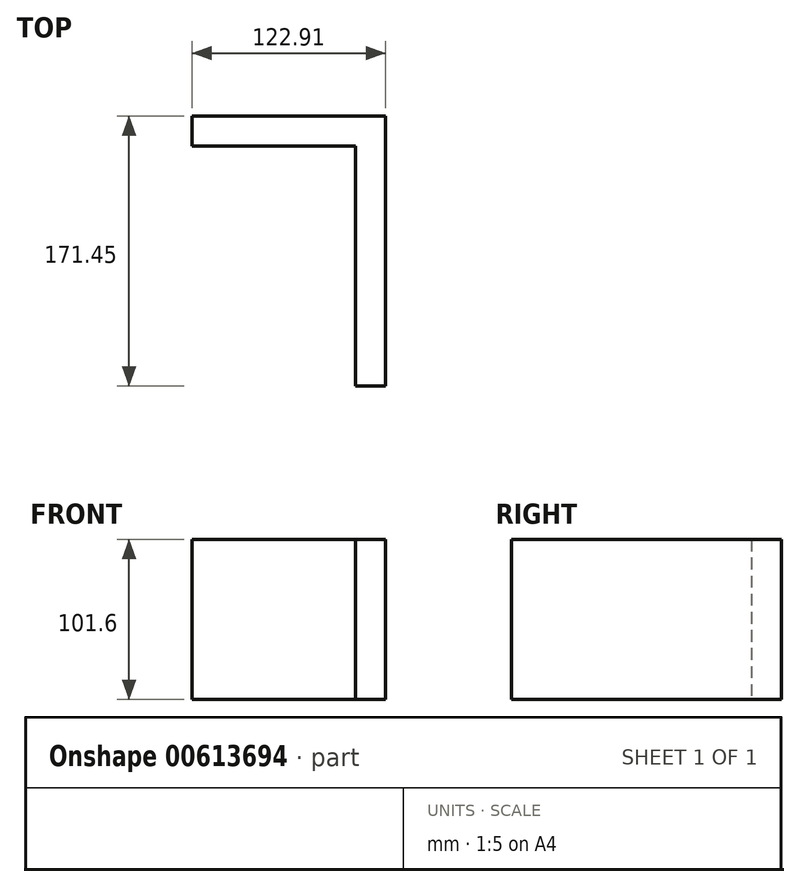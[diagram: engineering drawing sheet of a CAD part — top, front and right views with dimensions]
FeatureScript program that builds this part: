
annotation { "Feature Type Name" : "Feature", "Feature Type Description" : "" }
export const myFeature = defineFeature(function(context is Context, id is Id, definition is map)
    precondition{}
    {
        {
            var Q0;
            Q0=qCreatedBy(makeId("Top.planeOp"),FACE);
            var sketch = newSketch(context, id + "F0", { "sketchPlane" : qUnion([Q0])});
            skLineSegment(sketch, "E0.bottom", {"start": v(0, 0) * mm, "end": v(-122.9, 0) * mm});
            skLineSegment(sketch, "E0.top", {"start": v(0, 19.05) * mm, "end": v(-122.9, 19.05) * mm});
            skLineSegment(sketch, "E0.left", {"start": v(0, 0) * mm, "end": v(0, 19.05) * mm});
            skLineSegment(sketch, "E0.right", {"start": v(-122.9, 0) * mm, "end": v(-122.9, 19.05) * mm});
            skLineSegment(sketch, "E1.bottom", {"start": v(0, 0) * mm, "end": v(19.05, 0) * mm});
            skLineSegment(sketch, "E1.top", {"start": v(0, 152.4) * mm, "end": v(19.05, 152.4) * mm});
            skLineSegment(sketch, "E1.left", {"start": v(0, 0) * mm, "end": v(0, 152.4) * mm});
            skLineSegment(sketch, "E1.right", {"start": v(19.05, 0) * mm, "end": v(19.05, 152.4) * mm});
            skSolve(sketch);
        }
        {
            var Q0;
            {var subQ0=sQuery(id+"F0.wireOp",EDGE,"E0.bottom");Q0=makeQuery(id+"F0.imprint","IMPRINT",FACE,{"disambiguationData":[TD([[makeQuery(id+"F0.imprint","IMPRINT",EDGE,{"derivedFrom":subQ0}),-1.0]])]});}
            extrude(context, id + "F1", {"entities" : qUnion([Q0]), "depth" : 101.6 * mm, "offsetDistance" : 25.4 * mm});
        }
        {
            var Q0;
            Q0=makeQuery(id+"F1.opExtrude","SWEPT_FACE",FACE,{"disambiguationData":[OSD([sQuery(id+"F0.wireOp",EDGE,"E0.bottom")])]});
            var sketch = newSketch(context, id + "F2", { "sketchPlane" : qUnion([Q0])});
            skLineSegment(sketch, "E2.bottom", {"start": v(0, 101.6) * mm, "end": v(-19.05, 101.6) * mm});
            skLineSegment(sketch, "E2.top", {"start": v(0, 0) * mm, "end": v(-19.05, 0) * mm});
            skLineSegment(sketch, "E2.left", {"start": v(0, 101.6) * mm, "end": v(0, 0) * mm});
            skLineSegment(sketch, "E2.right", {"start": v(-19.05, 101.6) * mm, "end": v(-19.05, 0) * mm});
            skLineSegment(sketch, "E3", {"start": v(0, 50.8) * mm, "end": v(-122.9, 50.8) * mm});
            skLineSegment(sketch, "E4", {"start": v(-19.05, 57.15) * mm, "end": v(-19.05, 44.45) * mm});
            skLineSegment(sketch, "E5", {"start": v(0, 52.39) * mm, "end": v(0, 49.21) * mm});
            skLineSegment(sketch, "E6", {"start": v(0, 49.21) * mm, "end": v(0, 52.39) * mm});
            skLineSegment(sketch, "E7", {"start": v(-19.05, 57.15) * mm, "end": v(0, 52.39) * mm});
            skLineSegment(sketch, "E8", {"start": v(-19.05, 44.45) * mm, "end": v(0, 49.21) * mm});
            skLineSegment(sketch, "E9.0.1.0", {"start": v(-19.05, 76.2) * mm, "end": v(0, 71.44) * mm});
            skLineSegment(sketch, "E9.0.1.1", {"start": v(-19.05, 76.2) * mm, "end": v(-19.05, 63.5) * mm});
            skLineSegment(sketch, "E9.0.1.2", {"start": v(0, 68.26) * mm, "end": v(0, 71.44) * mm});
            skLineSegment(sketch, "E9.0.1.3", {"start": v(-19.05, 63.5) * mm, "end": v(0, 68.26) * mm});
            skLineSegment(sketch, "E9.0.2.0", {"start": v(-19.05, 95.25) * mm, "end": v(0, 90.49) * mm});
            skLineSegment(sketch, "E9.0.2.1", {"start": v(-19.05, 95.25) * mm, "end": v(-19.05, 82.55) * mm});
            skLineSegment(sketch, "E9.0.2.2", {"start": v(0, 87.31) * mm, "end": v(0, 90.49) * mm});
            skLineSegment(sketch, "E9.0.2.3", {"start": v(-19.05, 82.55) * mm, "end": v(0, 87.31) * mm});
            skLineSegment(sketch, "E9.0.3.0", {"start": v(-19.05, 114.3) * mm, "end": v(0, 109.54) * mm});
            skLineSegment(sketch, "E9.0.3.1", {"start": v(-19.05, 114.3) * mm, "end": v(-19.05, 101.6) * mm});
            skLineSegment(sketch, "E9.0.3.2", {"start": v(0, 106.36) * mm, "end": v(0, 109.54) * mm});
            skLineSegment(sketch, "E9.0.3.3", {"start": v(-19.05, 101.6) * mm, "end": v(0, 106.36) * mm});
            skLineSegment(sketch, "E9.direction1", {"start": v(-19.05, 44.45) * mm, "end": v(6.35, 44.45) * mm, "construction": true});
            skLineSegment(sketch, "E9.direction2", {"start": v(-19.05, 44.45) * mm, "end": v(-19.05, 63.5) * mm, "construction": true});
            skLineSegment(sketch, "E10.MirrorCS", {"start": v(-19.05, 25.4) * mm, "end": v(0, 30.16) * mm});
            skLineSegment(sketch, "E11.MirrorCS", {"start": v(-19.05, 38.1) * mm, "end": v(0, 33.34) * mm});
            skLineSegment(sketch, "E12.MirrorCS", {"start": v(-19.05, 19.05) * mm, "end": v(0, 14.29) * mm});
            skLineSegment(sketch, "E13.MirrorCS", {"start": v(-19.05, 6.35) * mm, "end": v(0, 11.11) * mm});
            skLineSegment(sketch, "E14.MirrorCS", {"start": v(-19.05, 0) * mm, "end": v(0, -4.76) * mm});
            skLineSegment(sketch, "E15.MirrorCS", {"start": v(-19.05, -12.7) * mm, "end": v(0, -7.94) * mm});
            skLineSegment(sketch, "E16", {"start": v(-19.05, 0) * mm, "end": v(-19.05, -12.7) * mm});
            skLineSegment(sketch, "E17", {"start": v(0, -4.76) * mm, "end": v(0, -7.94) * mm});
            skSolve(sketch);
        }
        {
            var Q0;
            Q0=makeQuery(id+"F2.imprint","IMPRINT",FACE,{"disambiguationData":[TD([[makeQuery(id+"F2.imprint","IMPRINT",EDGE,{"derivedFrom":sQuery(id+"F2.wireOp",EDGE,"E14.MirrorCS")}),-1.0]])]});
            var Q1;
            {var subQ0=sQuery(id+"F2.wireOp",EDGE,"E12.MirrorCS");Q1=makeQuery(id+"F2.imprint","IMPRINT",FACE,{"disambiguationData":[TD([[makeQuery(id+"F2.imprint","IMPRINT",EDGE,{"derivedFrom":subQ0}),-1.0]])]});}
            var Q2;
            Q2=makeQuery(id+"F2.imprint","IMPRINT",FACE,{"disambiguationData":[TD([[makeQuery(id+"F2.imprint","IMPRINT",EDGE,{"derivedFrom":sQuery(id+"F2.wireOp",EDGE,"E9.0.3.0")}),-1.0]])]});
            var Q3;
            Q3=makeQuery(id+"F2.imprint","IMPRINT",FACE,{"disambiguationData":[TD([[makeQuery(id+"F2.imprint","IMPRINT",EDGE,{"derivedFrom":sQuery(id+"F2.wireOp",EDGE,"E9.0.2.0")}),-1.0]])]});
            var Q4;
            Q4=makeQuery(id+"F2.imprint","IMPRINT",FACE,{"disambiguationData":[TD([[makeQuery(id+"F2.imprint","IMPRINT",EDGE,{"derivedFrom":sQuery(id+"F2.wireOp",EDGE,"E9.0.1.0")}),-1.0]])]});
            var Q5;
            {var subQ0=sQuery(id+"F2.wireOp",EDGE,"E10.MirrorCS");Q5=makeQuery(id+"F2.imprint","IMPRINT",FACE,{"disambiguationData":[TD([[makeQuery(id+"F2.imprint","IMPRINT",EDGE,{"derivedFrom":subQ0}),1.0]])]});}
            var Q6;
            {var subQ5=sQuery(id+"F2.wireOp",EDGE,"E7");Q6=makeQuery(id+"F2.imprint","IMPRINT",FACE,{"disambiguationData":[TD([[makeQuery(id+"F2.imprint","IMPRINT",EDGE,{"derivedFrom":subQ5}),-1.0]])]});}
            var Q7;
            {var subQ5=sQuery(id+"F2.wireOp",EDGE,"E8");Q7=makeQuery(id+"F2.imprint","IMPRINT",FACE,{"disambiguationData":[TD([[makeQuery(id+"F2.imprint","IMPRINT",EDGE,{"derivedFrom":subQ5}),1.0]])]});}
            extrude(context, id + "F3", {"entities" : qUnion([Q0, Q1, Q2, Q3, Q4, Q5, Q6, Q7]), "operationType" : NewBodyOperationType.REMOVE, "endBound" : BoundingType.THROUGH_ALL, "oppositeDirection" : true, "depth" : 25.4 * mm, "offsetDistance" : 25.4 * mm});
        }
        {
            var Q0;
            Q0=makeQuery(id+"F2.imprint","IMPRINT",FACE,{"disambiguationData":[TD([[makeQuery(id+"F2.imprint","IMPRINT",EDGE,{"derivedFrom":sQuery(id+"F2.wireOp",EDGE,"E9.0.2.0")}),-1.0]])]});
            var Q1;
            Q1=makeQuery(id+"F2.imprint","IMPRINT",FACE,{"disambiguationData":[TD([[makeQuery(id+"F2.imprint","IMPRINT",EDGE,{"derivedFrom":sQuery(id+"F2.wireOp",EDGE,"E9.0.1.0")}),-1.0]])]});
            var Q2;
            {var subQ5=sQuery(id+"F2.wireOp",EDGE,"E8");Q2=makeQuery(id+"F2.imprint","IMPRINT",FACE,{"disambiguationData":[TD([[makeQuery(id+"F2.imprint","IMPRINT",EDGE,{"derivedFrom":subQ5}),1.0]])]});}
            var Q3;
            {var subQ5=sQuery(id+"F2.wireOp",EDGE,"E7");Q3=makeQuery(id+"F2.imprint","IMPRINT",FACE,{"disambiguationData":[TD([[makeQuery(id+"F2.imprint","IMPRINT",EDGE,{"derivedFrom":subQ5}),-1.0]])]});}
            var Q4;
            {var subQ0=sQuery(id+"F2.wireOp",EDGE,"E10.MirrorCS");Q4=makeQuery(id+"F2.imprint","IMPRINT",FACE,{"disambiguationData":[TD([[makeQuery(id+"F2.imprint","IMPRINT",EDGE,{"derivedFrom":subQ0}),1.0]])]});}
            var Q5;
            {var subQ0=sQuery(id+"F2.wireOp",EDGE,"E12.MirrorCS");Q5=makeQuery(id+"F2.imprint","IMPRINT",FACE,{"disambiguationData":[TD([[makeQuery(id+"F2.imprint","IMPRINT",EDGE,{"derivedFrom":subQ0}),-1.0]])]});}
            var Q6;
            Q6=makeQuery(id+"F1.opExtrude","SWEPT_FACE",FACE,{"disambiguationData":[OSD([sQuery(id+"F0.wireOp",EDGE,"E0.top")])]});
            var Q7;
            Q7=makeQuery(id+"F1.opExtrude","CAP_VERTEX",VERTEX,{"disambiguationData":[OSD([sQuery(id+"F0.wireOp",EDGE,"E0.top"),sQuery(id+"F0.wireOp",EDGE,"E1.left")])],"isStart":false});
            extrude(context, id + "F4", {"entities" : qUnion([Q0, Q1, Q2, Q3, Q4, Q5]), "endBound" : BoundingType.UP_TO_VERTEX, "oppositeDirection" : true, "depth" : 25.4 * mm, "endBoundEntityFace" : qUnion([Q6]), "endBoundEntityVertex" : qUnion([Q7]), "offsetDistance" : 25.4 * mm});
        }
        {
            var Q0;
            {var subQ0=sQuery(id+"F2.wireOp",EDGE,"E2.bottom");Q0=makeQuery(id+"F2.imprint","IMPRINT",FACE,{"disambiguationData":[TD([[makeQuery(id+"F2.imprint","IMPRINT",EDGE,{"derivedFrom":subQ0}),1.0]])]});}
            var Q1;
            Q1=makeQuery(id+"F2.imprint","IMPRINT",FACE,{"disambiguationData":[TD([[makeQuery(id+"F2.imprint","IMPRINT",EDGE,{"derivedFrom":sQuery(id+"F2.wireOp",EDGE,"E9.0.2.0")}),-1.0]])]});
            var Q2;
            {var subQ0=sQuery(id+"F2.wireOp",EDGE,"E9.0.1.0");Q2=makeQuery(id+"F2.imprint","IMPRINT",FACE,{"disambiguationData":[TD([[makeQuery(id+"F2.imprint","IMPRINT",EDGE,{"derivedFrom":subQ0}),1.0]])]});}
            var Q3;
            Q3=makeQuery(id+"F2.imprint","IMPRINT",FACE,{"disambiguationData":[TD([[makeQuery(id+"F2.imprint","IMPRINT",EDGE,{"derivedFrom":sQuery(id+"F2.wireOp",EDGE,"E9.0.1.0")}),-1.0]])]});
            var Q4;
            {var subQ0=sQuery(id+"F2.wireOp",EDGE,"E7");Q4=makeQuery(id+"F2.imprint","IMPRINT",FACE,{"disambiguationData":[TD([[makeQuery(id+"F2.imprint","IMPRINT",EDGE,{"derivedFrom":subQ0}),1.0]])]});}
            var Q5;
            {var subQ5=sQuery(id+"F2.wireOp",EDGE,"E7");Q5=makeQuery(id+"F2.imprint","IMPRINT",FACE,{"disambiguationData":[TD([[makeQuery(id+"F2.imprint","IMPRINT",EDGE,{"derivedFrom":subQ5}),-1.0]])]});}
            var Q6;
            {var subQ2=sQuery(id+"F2.wireOp",EDGE,"E11.MirrorCS");Q6=makeQuery(id+"F2.imprint","IMPRINT",FACE,{"disambiguationData":[TD([[makeQuery(id+"F2.imprint","IMPRINT",EDGE,{"derivedFrom":subQ2}),1.0]])]});}
            var Q7;
            {var subQ0=sQuery(id+"F2.wireOp",EDGE,"E10.MirrorCS");Q7=makeQuery(id+"F2.imprint","IMPRINT",FACE,{"disambiguationData":[TD([[makeQuery(id+"F2.imprint","IMPRINT",EDGE,{"derivedFrom":subQ0}),1.0]])]});}
            var Q8;
            {var subQ5=sQuery(id+"F2.wireOp",EDGE,"E8");Q8=makeQuery(id+"F2.imprint","IMPRINT",FACE,{"disambiguationData":[TD([[makeQuery(id+"F2.imprint","IMPRINT",EDGE,{"derivedFrom":subQ5}),1.0]])]});}
            var Q9;
            {var subQ0=sQuery(id+"F2.wireOp",EDGE,"E10.MirrorCS");Q9=makeQuery(id+"F2.imprint","IMPRINT",FACE,{"disambiguationData":[TD([[makeQuery(id+"F2.imprint","IMPRINT",EDGE,{"derivedFrom":subQ0}),-1.0]])]});}
            var Q10;
            {var subQ0=sQuery(id+"F2.wireOp",EDGE,"E12.MirrorCS");Q10=makeQuery(id+"F2.imprint","IMPRINT",FACE,{"disambiguationData":[TD([[makeQuery(id+"F2.imprint","IMPRINT",EDGE,{"derivedFrom":subQ0}),-1.0]])]});}
            var Q11;
            {var subQ0=sQuery(id+"F2.wireOp",EDGE,"E2.top");Q11=makeQuery(id+"F2.imprint","IMPRINT",FACE,{"disambiguationData":[TD([[makeQuery(id+"F2.imprint","IMPRINT",EDGE,{"derivedFrom":subQ0}),-1.0]])]});}
            extrude(context, id + "F5", {"entities" : qUnion([Q0, Q1, Q2, Q3, Q4, Q5, Q6, Q7, Q8, Q9, Q10, Q11]), "operationType" : NewBodyOperationType.ADD, "depth" : 152.4 * mm, "offsetDistance" : 25.4 * mm});
        }
    });
